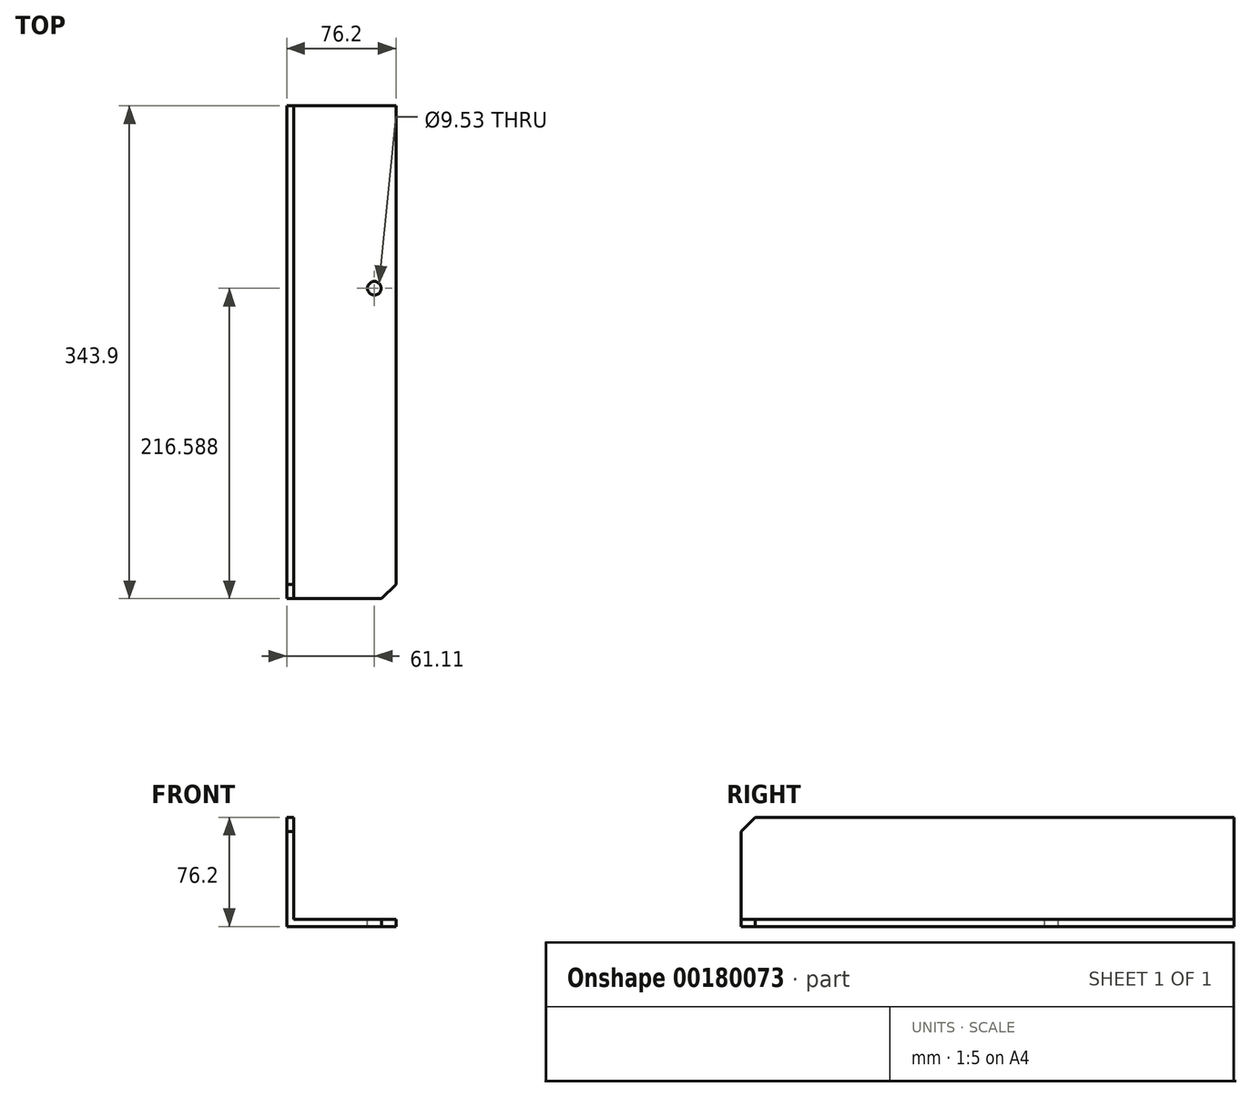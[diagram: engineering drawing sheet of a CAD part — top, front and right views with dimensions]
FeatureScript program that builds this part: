
annotation { "Feature Type Name" : "Feature", "Feature Type Description" : "" }
export const myFeature = defineFeature(function(context is Context, id is Id, definition is map)
    precondition{}
    {
        {
            var Q0;
            Q0=qCreatedBy(makeId("Front.planeOp"),FACE);
            var sketch = newSketch(context, id + "F0", { "sketchPlane" : qUnion([Q0])});
            skLineSegment(sketch, "E0", {"start": v(0, 0) * mm, "end": v(76.2, 0) * mm});
            skLineSegment(sketch, "E1", {"start": v(0, 0) * mm, "end": v(0, 76.2) * mm});
            skLineSegment(sketch, "E2.0", {"start": v(5, 5) * mm, "end": v(5, 76.2) * mm});
            skLineSegment(sketch, "E2.1", {"start": v(5, 5) * mm, "end": v(76.2, 5) * mm});
            skLineSegment(sketch, "E3", {"start": v(0, 76.2) * mm, "end": v(5, 76.2) * mm});
            skLineSegment(sketch, "E4", {"start": v(76.2, 0) * mm, "end": v(76.2, 5) * mm});
            skSolve(sketch);
        }
        {
            var Q0;
            Q0=makeQuery(id+"F0.imprint","IMPRINT",FACE,{"disambiguationData":[TD([[makeQuery(id+"F0.imprint","IMPRINT",EDGE,{"derivedFrom":sQuery(id+"F0.wireOp",EDGE,"E0")}),1.0]])]});
            extrude(context, id + "F1", {"entities" : qUnion([Q0]), "depth" : 343.9 * mm});
        }
        {
            var Q0;
            Q0=makeQuery(id+"F1.opExtrude","CAP_EDGE",EDGE,{"disambiguationData":[OSD([sQuery(id+"F0.wireOp",EDGE,"E4")])],"isStart":false});
            var Q1;
            Q1=makeQuery(id+"F1.opExtrude","CAP_EDGE",EDGE,{"disambiguationData":[OSD([sQuery(id+"F0.wireOp",EDGE,"E3")])],"isStart":false});
            chamfer(context, id + "F2", {"entities" : qUnion([Q0, Q1]), "width" : 10 * mm, "tangentPropagation" : true});
        }
        {
            var Q0;
            Q0=makeQuery(id+"F1.opExtrude","SWEPT_FACE",FACE,{"disambiguationData":[OSD([sQuery(id+"F0.wireOp",EDGE,"E2.1")])]});
            var sketch = newSketch(context, id + "F3", { "sketchPlane" : qUnion([Q0])});
            skLineSegment(sketch, "E5.0", {"start": v(5, -127.31) * mm, "end": v(66.2, -127.31) * mm});
            skLineSegment(sketch, "E6.0", {"start": v(65.16, -341.4) * mm, "end": v(73.7, -332.86) * mm});
            skLineSegment(sketch, "E6.1", {"start": v(7.5, -341.4) * mm, "end": v(65.16, -341.4) * mm});
            skLineSegment(sketch, "E6.2", {"start": v(73.7, -332.86) * mm, "end": v(73.7, -2.5) * mm});
            skLineSegment(sketch, "E6.3", {"start": v(73.7, -2.5) * mm, "end": v(7.5, -2.5) * mm});
            skLineSegment(sketch, "E6.4", {"start": v(7.5, -2.5) * mm, "end": v(7.5, -341.4) * mm});
            skLineSegment(sketch, "E7.0", {"start": v(61.1, -333.9) * mm, "end": v(61.1, 0) * mm});
            skLineSegment(sketch, "E8.2", {"start": v(46.87, -29.33) * mm, "end": v(34.33, -29.33) * mm});
            skPoint(sketch, "E9", {"position": v(61.1, -127.31) * mm});
            skSolve(sketch);
        }
        {
            var Q0;
            Q0=sQuery(id+"F3.wireOp",VERTEX,"E9");
            var Q1;
            Q1=makeQuery(id+"F1.opExtrude","SWEPT_BODY",BODY,{"disambiguationData":[OSD([sQuery(id+"F0.wireOp",EDGE,"E0"),sQuery(id+"F0.wireOp",EDGE,"E1"),sQuery(id+"F0.wireOp",EDGE,"E2.0"),sQuery(id+"F0.wireOp",EDGE,"E2.1"),sQuery(id+"F0.wireOp",EDGE,"E3"),sQuery(id+"F0.wireOp",EDGE,"E4")])]});
            hole(context, id + "F4", {"style" : HoleStyle.SIMPLE, "endStyle" : HoleEndStyle.THROUGH, "holeDiameter" : 9.53 * mm, "locations" : qUnion([Q0]), "scope" : qUnion([Q1]), "isTappedThrough" : true});
        }
    });
